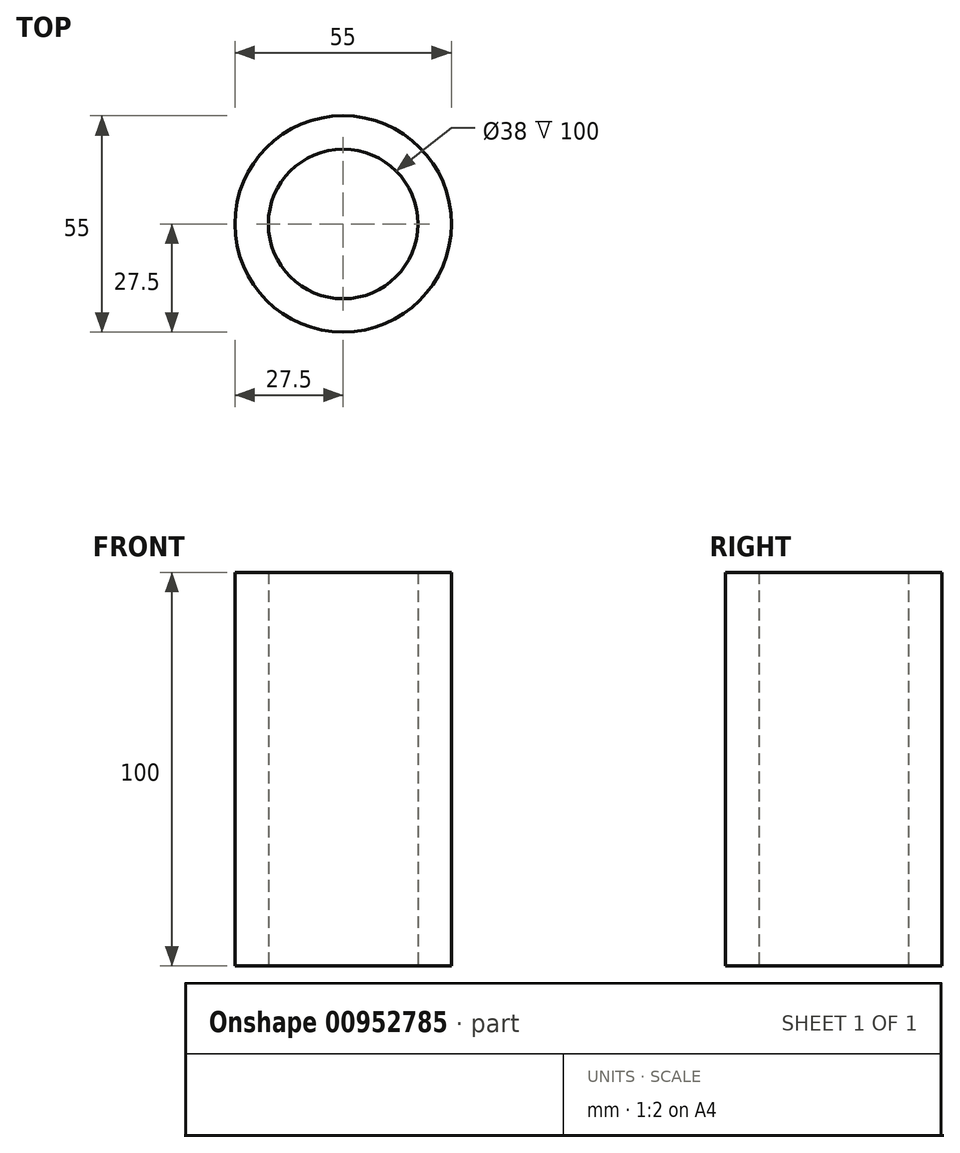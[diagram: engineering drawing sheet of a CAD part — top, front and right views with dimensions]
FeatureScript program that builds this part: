
annotation { "Feature Type Name" : "Feature", "Feature Type Description" : "" }
export const myFeature = defineFeature(function(context is Context, id is Id, definition is map)
    precondition{}
    {
        {
            var Q0;
            Q0=qCreatedBy(makeId("Top.planeOp"),FACE);
            var sketch = newSketch(context, id + "F0", { "sketchPlane" : qUnion([Q0])});
            skCircle(sketch, "E0", {"center": v(0, 0) * mm, "radius": 27.5 * mm});
            skSolve(sketch);
        }
        {
            var Q0;
            Q0 = qSketchRegion(id + "F0", true);
            extrude(context, id + "F1", {"entities" : qUnion([Q0]), "endBound" : BoundingType.SYMMETRIC, "depth" : 100 * mm, "offsetDistance" : 25 * mm});
        }
        {
            var Q0;
            Q0=makeQuery(id+"F1.opExtrude","CAP_FACE",FACE,{"disambiguationData":[OSD([sQuery(id+"F0.wireOp",EDGE,"E0")])],"isStart":true});
            var sketch = newSketch(context, id + "F2", { "sketchPlane" : qUnion([Q0])});
            skPoint(sketch, "E1", {"position": v(0, 0) * mm});
            skSolve(sketch);
        }
        {
            var Q0;
            Q0=sQuery(id+"F2.wireOp",VERTEX,"E1");
            var Q1;
            Q1=makeQuery(id+"F1.opExtrude","SWEPT_BODY",BODY,{"disambiguationData":[OSD([sQuery(id+"F0.wireOp",EDGE,"E0")])]});
            hole(context, id + "F3", {"style" : HoleStyle.SIMPLE, "endStyle" : HoleEndStyle.THROUGH, "holeDiameter" : 38 * mm, "majorDiameter" : 5 * mm, "isTappedThrough" : true, "tappedDepth" : 12 * mm, "tapClearance" : 3, "startFromSketch" : true, "locations" : qUnion([Q0]), "scope" : qUnion([Q1])});
        }
    });
